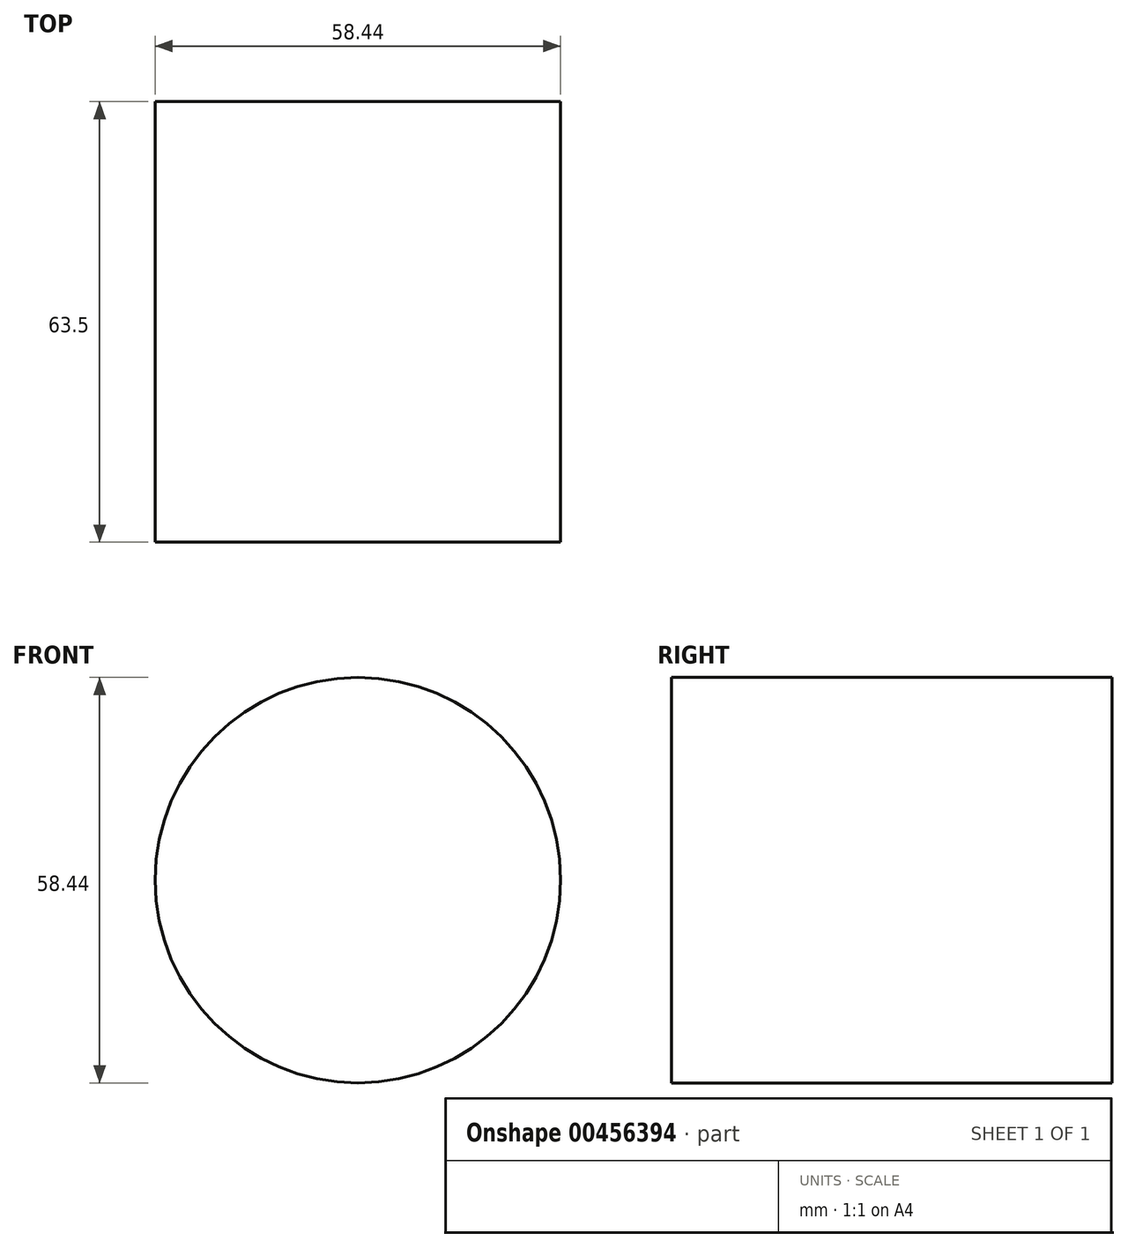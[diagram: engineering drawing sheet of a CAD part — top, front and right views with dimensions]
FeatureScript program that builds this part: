
annotation { "Feature Type Name" : "Feature", "Feature Type Description" : "" }
export const myFeature = defineFeature(function(context is Context, id is Id, definition is map)
    precondition{}
    {
        {
            var Q0;
            Q0=qCreatedBy(makeId("Front.planeOp"),FACE);
            var sketch = newSketch(context, id + "F0", { "sketchPlane" : qUnion([Q0])});
            skCircle(sketch, "E0", {"center": v(0, 0) * mm, "radius": 29.22 * mm});
            skSolve(sketch);
        }
        {
            var Q0;
            Q0=sQuery(id+"F0.wireOp",EDGE,"E0");
            extrude(context, id + "F1", {"bodyType" : ToolBodyType.SURFACE, "surfaceEntities" : qUnion([Q0]), "depth" : 63.5 * mm});
        }
    });
